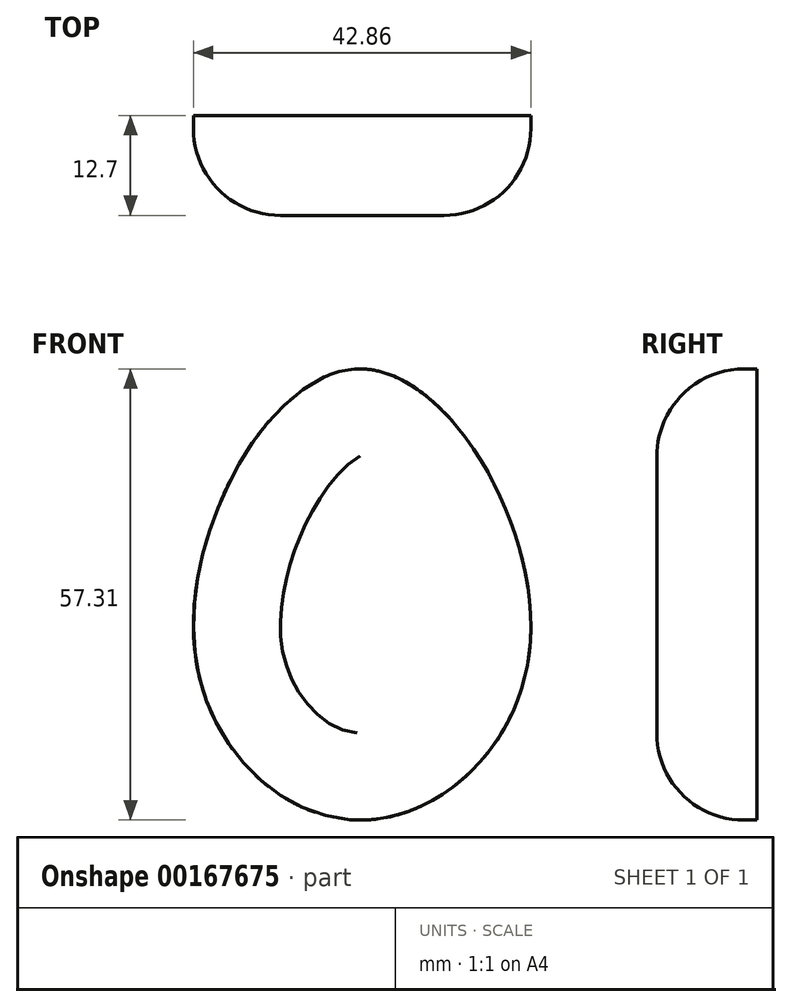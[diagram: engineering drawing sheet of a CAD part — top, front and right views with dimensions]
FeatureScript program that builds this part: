
annotation { "Feature Type Name" : "Feature", "Feature Type Description" : "" }
export const myFeature = defineFeature(function(context is Context, id is Id, definition is map)
    precondition{}
    {
        {
            var Q0;
            Q0=qCreatedBy(makeId("Front.planeOp"),FACE);
            var sketch = newSketch(context, id + "F0", { "sketchPlane" : qUnion([Q0])});
            skFitSpline(sketch, "E0", {"points": [v(21.7, 0) * mm, v(0, 34.62) * mm, v(-21.04, 0) * mm, v(0, -22.7) * mm, v(21.7, 0) * mm]});
            skSolve(sketch);
        }
        {
            var Q0;
            Q0=qSketchRegion(id+"F0",true);
            extrude(context, id + "F1", {"entities" : qUnion([Q0]), "depth" : 12.7 * mm});
        }
        {
            var Q0;
            Q0=makeQuery(id+"F1.opExtrude","CAP_EDGE",EDGE,{"disambiguationData":[OSD([sQuery(id+"F0.wireOp",EDGE,"E0")])],"isStart":false});
            fillet(context, id + "F2", {"entities" : qUnion([Q0]), "radius" : 11.04 * mm, "tangentPropagation" : true, "allowEdgeOverflow" : false});
        }
    });
